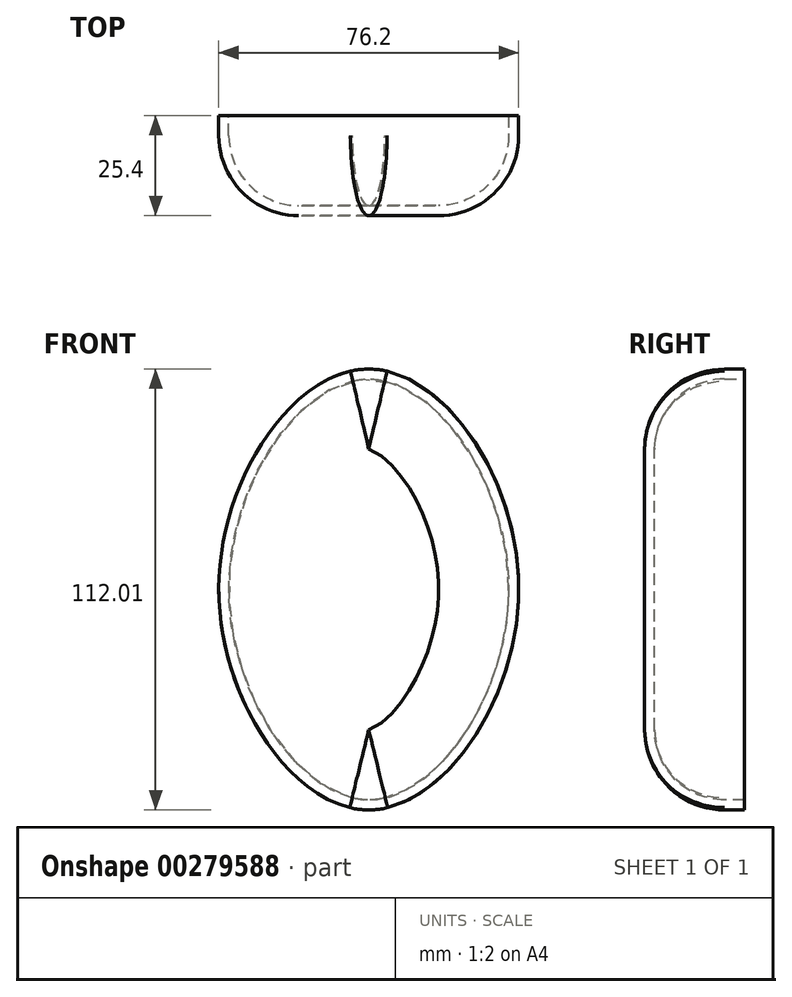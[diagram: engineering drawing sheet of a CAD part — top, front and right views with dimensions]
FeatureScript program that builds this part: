
annotation { "Feature Type Name" : "Feature", "Feature Type Description" : "" }
export const myFeature = defineFeature(function(context is Context, id is Id, definition is map)
    precondition{}
    {
        {
            var Q0;
            Q0=qCreatedBy(makeId("Front.planeOp"),FACE);
            var sketch = newSketch(context, id + "F0", { "sketchPlane" : qUnion([Q0])});
            skFitSpline(sketch, "E0", {"points": [v(-38.1, 0) * mm, v(0, -56.24) * mm, v(38.1, 0) * mm, v(0, 55.77) * mm, v(-38.1, 0) * mm]});
            skSolve(sketch);
        }
        {
            var Q0;
            Q0=makeQuery(id+"F0.imprint","IMPRINT",FACE,{"disambiguationData":[TD([[makeQuery(id+"F0.imprint","IMPRINT",EDGE,{"derivedFrom":sQuery(id+"F0.wireOp",EDGE,"E0")}),1.0]])]});
            extrude(context, id + "F1", {"entities" : qUnion([Q0]), "depth" : 25.4 * mm});
        }
        {
            var Q0;
            Q0=makeQuery(id+"F1.opExtrude","CAP_EDGE",EDGE,{"disambiguationData":[OSD([sQuery(id+"F0.wireOp",EDGE,"E0")])],"isStart":false});
            fillet(context, id + "F2", {"entities" : qUnion([Q0]), "radius" : 20.32 * mm, "tangentPropagation" : true, "allowEdgeOverflow" : false});
        }
        {
            var Q0;
            Q0=makeQuery(id+"F1.opExtrude","CAP_FACE",FACE,{"disambiguationData":[OSD([sQuery(id+"F0.wireOp",EDGE,"E0")])],"isStart":true});
            shell(context, id + "F3", {"entities" : qUnion([Q0]), "thickness" : 2.54 * mm});
        }
    });
